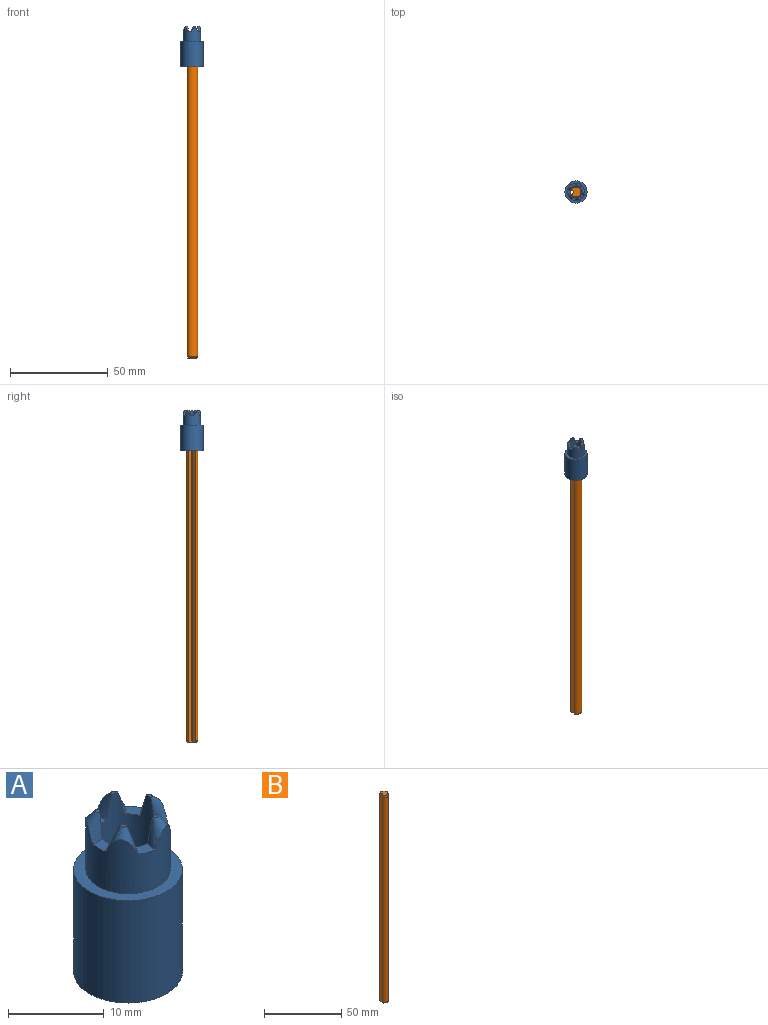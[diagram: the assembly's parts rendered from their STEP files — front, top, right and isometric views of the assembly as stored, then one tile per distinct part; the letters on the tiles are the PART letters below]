
ASSEMBLY  parts=2 mates=1
PART A: 20 faces, bbox 11.7x11.7x21.3 mm
  f0: cone r=1.8mm half-angle=24.8deg, axis (0.34,0,-0.94), area 9.2mm2, adj f1,f2,f3,f4,f16
  f1: plane 0.98x0.75mm, normal (0,0,1), area 0.2mm2, adj f0,f2
  f2: cylinder r=3.04mm len=20.85mm, axis (0,0,-1), area 363.1mm2, adj f0,f1,f4,f5,f6,f7,f8,f9
  f3: cylinder r=4.4mm len=8.8mm, axis (0,0,-1), area 159.2mm2, adj f0,f4,f6,f7,f9,f10,f12,f13
  f4: plane 2.34x2.24mm, normal (0,0,1), area 2.3mm2, adj f0,f2,f3,f6
  f5: plane 0.98x0.84mm, normal (0,0,1), area 0.2mm2, adj f2,f6
  f6: cone r=1.8mm half-angle=24.8deg, axis (0.11,0.33,-0.94), area 9.2mm2, adj f2,f3,f4,f5,f7
  f7: plane 2.22x1.93mm, normal (0,0,1), area 2.3mm2, adj f2,f3,f6,f9
  f8: plane 0.96x0.91mm, normal (0,0,1), area 0.2mm2, adj f2,f9
  f9: cone r=1.8mm half-angle=24.8deg, axis (-0.28,0.2,-0.94), area 9.2mm2, adj f2,f3,f7,f8,f10
  f10: plane 2.02x1.55mm, normal (0,0,1), area 2.3mm2, adj f2,f3,f9,f12
  f11: plane 0.96x0.91mm, normal (0,0,1), area 0.2mm2, adj f2,f12
  f12: cone r=1.8mm half-angle=24.8deg, axis (-0.28,-0.2,-0.94), area 9.2mm2, adj f2,f3,f10,f11,f13
  f13: plane 2.22x1.93mm, normal (0,0,1), area 2.3mm2, adj f2,f3,f12,f14
  f14: cone r=1.8mm half-angle=24.8deg, axis (0.11,-0.33,-0.94), area 9.2mm2, adj f2,f3,f13,f15,f16
  f15: plane 0.98x0.84mm, normal (0,0,1), area 0.2mm2, adj f2,f14
  f16: plane 2.34x2.24mm, normal (0,0,1), area 2.3mm2, adj f0,f2,f3,f14
  f17: cylinder r=5.68mm len=13.05mm, axis (0,0,1), area 465.3mm2, adj f18,f19
  f18: plane 11.35x11.35mm, normal (0,0,-1), area 72.1mm2, adj f2,f17
  f19: plane 11.35x11.35mm, normal (0,0,1), area 40.4mm2, adj f3,f17
PART B: 8 faces, bbox 5.6x5.9x165 mm
  f0: plane 165.02x1.36mm, normal (-0.71,0.71,0), area 311.6mm2, adj f1,f3,f4,f5,f6,f7
  f1: cylinder r=2.95mm len=162.9mm, axis (0,0,-1), area 2482.7mm2, adj f0,f2,f6,f7
  f2: plane 165.02x1.36mm, normal (-0.71,-0.71,0), area 311.6mm2, adj f1,f3,f4,f5,f6,f7
  f3: cylinder r=0.3mm len=165mm, axis (0,0,-1), area 77.8mm2, adj f0,f2,f4,f5
  f4: plane 5.09x4.75mm, normal (0,0,1), area 18.2mm2, adj f0,f2,f3,f7
  f5: plane 4.69x4.41mm, normal (0,0,-1), area 15.6mm2, adj f0,f2,f3,f6
  f6: cone r=2.95mm half-angle=45deg, axis (0,0,1), area 11.7mm2, adj f0,f1,f2,f5
  f7: cone r=2.54mm half-angle=15deg, axis (0,0,-1), area 22.2mm2, adj f0,f1,f2,f4
PLACE A at identity fixed
PLACE B t=(0,0,-162.15)mm
MATE fastened B.f1 <-> A.f2  axis (0,0,1) through (0,0,2.85)mm
